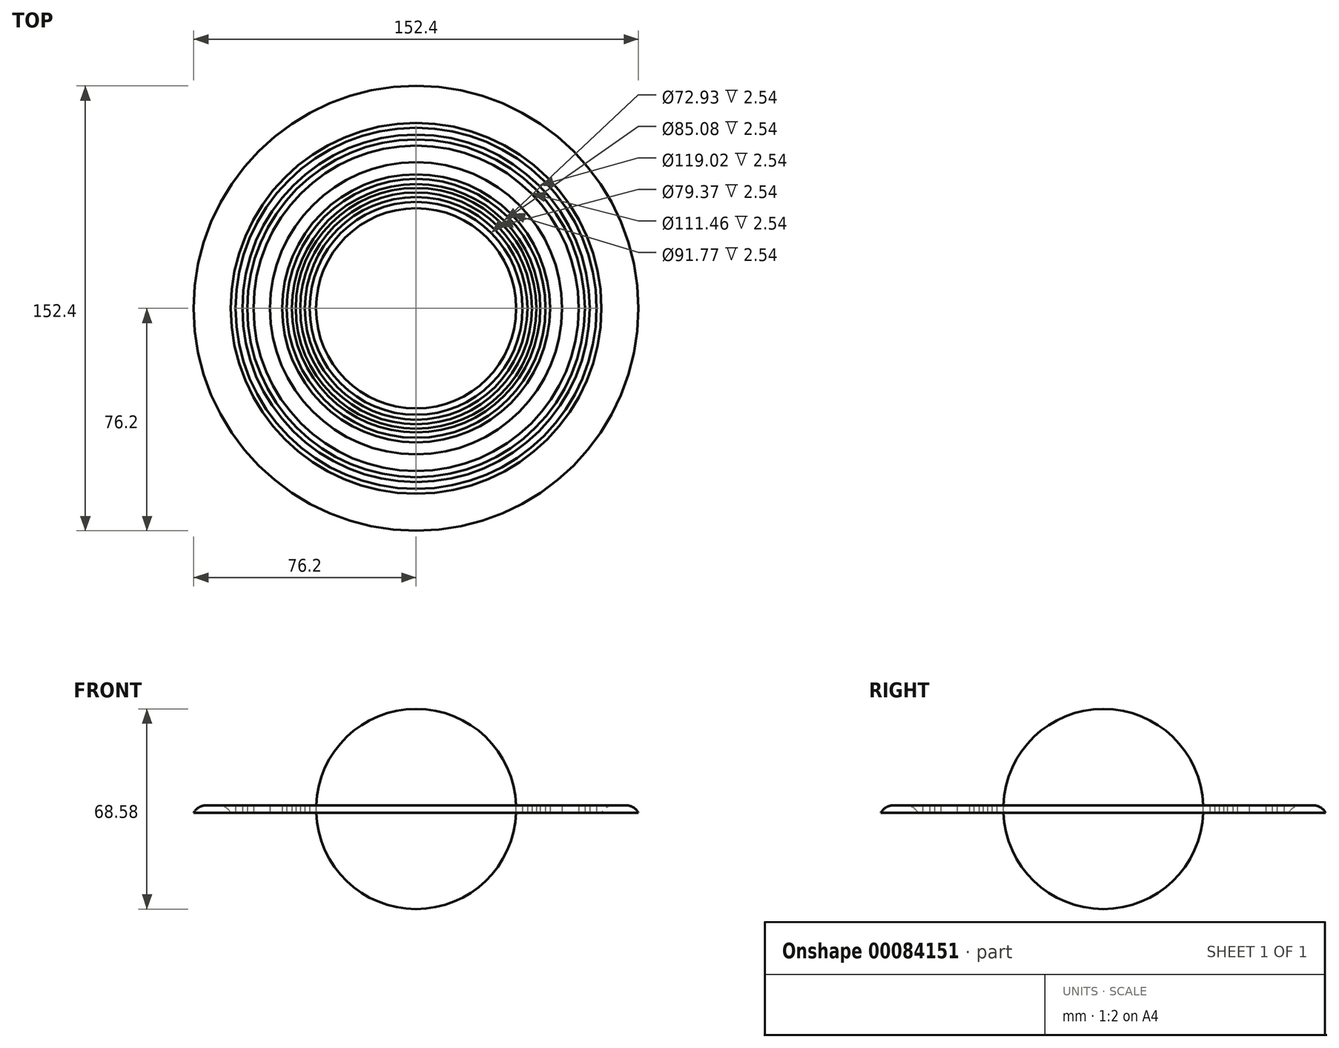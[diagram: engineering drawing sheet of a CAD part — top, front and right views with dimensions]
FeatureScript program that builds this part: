
annotation { "Feature Type Name" : "Feature", "Feature Type Description" : "" }
export const myFeature = defineFeature(function(context is Context, id is Id, definition is map)
    precondition{}
    {
        {
            var Q0;
            Q0=qCreatedBy(makeId("Front.planeOp"),FACE);
            var sketch = newSketch(context, id + "F0", { "sketchPlane" : qUnion([Q0])});
            skArc(sketch, "E0", {"start": v(0, 34.3) * mm, "mid": v(-34.3, 0) * mm, "end": v(0, -34.3) * mm});
            skLineSegment(sketch, "E1", {"start": v(0, -34.3) * mm, "end": v(0, 34.3) * mm});
            skSolve(sketch);
        }
        {
            var Q0;
            Q0=makeQuery(id+"F0.imprint","IMPRINT",FACE,{"disambiguationData":[TD([[makeQuery(id+"F0.imprint","IMPRINT",EDGE,{"derivedFrom":sQuery(id+"F0.wireOp",EDGE,"E0")}),1.0]])]});
            var sketch = newSketch(context, id + "F1", { "sketchPlane" : qUnion([Q0])});
            skSolve(sketch);
        }
        {
            var Q0;
            Q0 = qSketchRegion(id + "F1", true);
            var Q1;
            Q1=makeQuery(id+"F0.imprint","IMPRINT",FACE,{"disambiguationData":[TD([[makeQuery(id+"F0.imprint","IMPRINT",EDGE,{"derivedFrom":sQuery(id+"F0.wireOp",EDGE,"E0")}),1.0]])]});
            var Q2;
            Q2=sQuery(id+"F0.wireOp",EDGE,"E1");
            revolve(context, id + "F2", {"entities" : qUnion([Q0, Q1]), "axis" : qUnion([Q2]), "revolveType" : RevolveType.FULL});
        }
        {
            var Q0;
            Q0=qCreatedBy(makeId("Top.planeOp"),FACE);
            var sketch = newSketch(context, id + "F3", { "sketchPlane" : qUnion([Q0])});
            skCircle(sketch, "E2", {"center": v(0, 0) * mm, "radius": 63.5 * mm});
            skCircle(sketch, "E3", {"center": v(0, 0) * mm, "radius": 76.2 * mm});
            skCircle(sketch, "E4", {"center": v(0, 0) * mm, "radius": 61.86 * mm});
            skCircle(sketch, "E5", {"center": v(0, 0) * mm, "radius": 59.51 * mm});
            skCircle(sketch, "E6", {"center": v(0, 0) * mm, "radius": 57.82 * mm});
            skCircle(sketch, "E7", {"center": v(0, 0) * mm, "radius": 55.73 * mm});
            skCircle(sketch, "E8", {"center": v(0, 0) * mm, "radius": 50.04 * mm});
            skCircle(sketch, "E9", {"center": v(0, 0) * mm, "radius": 45.89 * mm});
            skCircle(sketch, "E10", {"center": v(0, 0) * mm, "radius": 44.34 * mm});
            skCircle(sketch, "E11", {"center": v(0, 0) * mm, "radius": 42.54 * mm});
            skCircle(sketch, "E12", {"center": v(0, 0) * mm, "radius": 41.24 * mm});
            skCircle(sketch, "E13", {"center": v(0, 0) * mm, "radius": 39.68 * mm});
            skCircle(sketch, "E14", {"center": v(0, 0) * mm, "radius": 38.13 * mm});
            skCircle(sketch, "E15", {"center": v(0, 0) * mm, "radius": 36.46 * mm});
            skSolve(sketch);
        }
        {
            var Q0;
            Q0 = qSketchRegion(id + "F3", true);
            var Q1;
            Q1=makeQuery(id+"F3.imprint","IMPRINT",FACE,{"disambiguationData":[TD([[makeQuery(id+"F3.imprint","IMPRINT",EDGE,{"derivedFrom":sQuery(id+"F3.wireOp",EDGE,"E4")}),1.0]])]});
            var Q2;
            Q2=makeQuery(id+"F3.imprint","IMPRINT",FACE,{"disambiguationData":[TD([[makeQuery(id+"F3.imprint","IMPRINT",EDGE,{"derivedFrom":sQuery(id+"F3.wireOp",EDGE,"E6")}),1.0]])]});
            var Q3;
            Q3=makeQuery(id+"F3.imprint","IMPRINT",FACE,{"disambiguationData":[TD([[makeQuery(id+"F3.imprint","IMPRINT",EDGE,{"derivedFrom":sQuery(id+"F3.wireOp",EDGE,"E8")}),1.0]])]});
            var Q4;
            Q4=makeQuery(id+"F3.imprint","IMPRINT",FACE,{"disambiguationData":[TD([[makeQuery(id+"F3.imprint","IMPRINT",EDGE,{"derivedFrom":sQuery(id+"F3.wireOp",EDGE,"E10")}),1.0]])]});
            var Q5;
            Q5=makeQuery(id+"F3.imprint","IMPRINT",FACE,{"disambiguationData":[TD([[makeQuery(id+"F3.imprint","IMPRINT",EDGE,{"derivedFrom":sQuery(id+"F3.wireOp",EDGE,"E12")}),1.0]])]});
            var Q6;
            Q6=makeQuery(id+"F3.imprint","IMPRINT",FACE,{"disambiguationData":[TD([[makeQuery(id+"F3.imprint","IMPRINT",EDGE,{"derivedFrom":sQuery(id+"F3.wireOp",EDGE,"E14")}),1.0]])]});
            extrude(context, id + "F4", {"entities" : qUnion([Q0, Q1, Q2, Q3, Q4, Q5, Q6]), "endBound" : BoundingType.SYMMETRIC, "depth" : 2.54 * mm});
        }
        {
            var Q0;
            Q0=makeQuery(id+"F4.opExtrude","CAP_FACE",FACE,{"disambiguationData":[OSD([sQuery(id+"F3.wireOp",EDGE,"E2"),sQuery(id+"F3.wireOp",EDGE,"E3")])],"isStart":false});
            fillet(context, id + "F5", {"entities" : qUnion([Q0]), "radius" : 5.08 * mm, "tangentPropagation" : true, "allowEdgeOverflow" : false});
        }
    });
